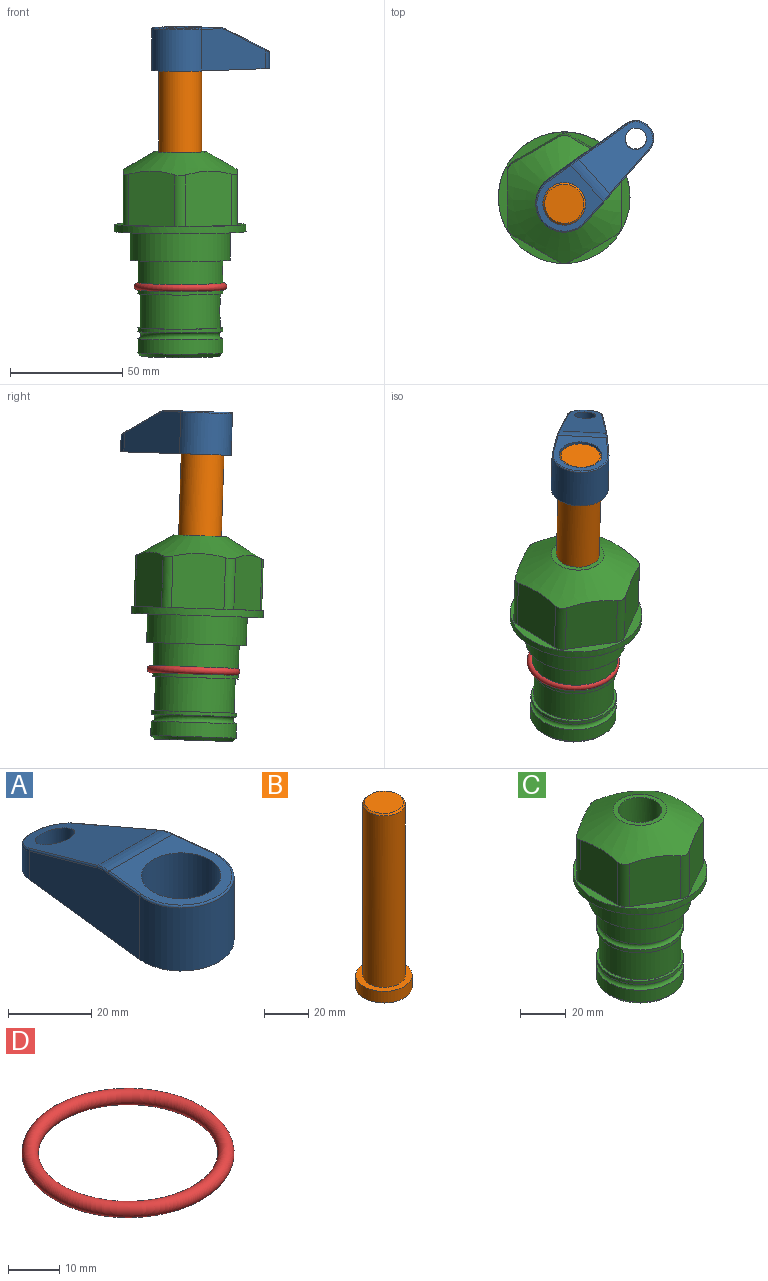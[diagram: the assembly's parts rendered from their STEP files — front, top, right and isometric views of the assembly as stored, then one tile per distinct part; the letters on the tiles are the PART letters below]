
ASSEMBLY  parts=4 mates=2
PART A: 44 faces, bbox 27.5x64.5x19.1 mm
  f0: plane 2.3x0.95mm, normal (0,0,-1), area 1mm2, adj f25,f30,f34
  f1: plane 63.5x25.4mm, normal (0,0,-1), area 561.7mm2, adj f2,f3,f4,f5,f6,f7,f19,f20
  f2: cylinder r=12.7mm len=25.4mm, axis (0,0,-1), area 792.2mm2, adj f1,f3,f5,f13
  f3: plane 42.33x18.54mm, normal (0.99,0.11,0), area 647mm2, adj f1,f2,f4,f11,f12,f14
  f4: cylinder r=7.94mm len=15.78mm, axis (0,0,-1), area 158.6mm2, adj f1,f3,f5,f16
  f5: plane 42.33x18.54mm, normal (-0.99,0.11,0), area 647mm2, adj f1,f2,f4,f15,f17,f18
  f6: cylinder r=9.53mm len=19.05mm, axis (0,0,-1), area 1140.1mm2, adj f1,f8
  f7: cylinder r=4.76mm len=10.98mm, axis (0,0,-1), area 276.1mm2, adj f1,f9
  f8: plane 25.83x24.38mm, normal (0,0,1), area 262.2mm2, adj f6,f10,f11,f13,f15
  f9: plane 32.49x20.55mm, normal (0,0.34,0.94), area 489.9mm2, adj f7,f10,f14,f16,f18
  f10: cylinder r=12.7mm len=21.49mm, axis (-1,0,0), area 93.2mm2, adj f8,f9,f12,f17
  f11: cylinder r=0.51mm len=12.34mm, axis (0.11,-0.99,0), area 9.9mm2, adj f3,f8,f12,f13
  f12: bspline ~7.62x1.64mm, area 3.5mm2, adj f3,f10,f11,f14
  f13: torus R=12.19mm, axis (0,0,1), area 33.6mm2, adj f2,f8,f11,f15
  f14: cylinder r=0.51mm len=26.01mm, axis (0.1,-0.93,0.34), area 21.6mm2, adj f3,f9,f12,f16
  f15: cylinder r=0.51mm len=12.34mm, axis (0.11,0.99,0), area 9.9mm2, adj f5,f8,f13,f17
  f16: bspline ~15.78x7.05mm, area 15.7mm2, adj f4,f9,f14,f18
  f17: bspline ~7.62x1.64mm, area 3.5mm2, adj f5,f10,f15,f18
  f18: cylinder r=0.51mm len=26.01mm, axis (0.1,0.93,-0.34), area 21.6mm2, adj f5,f9,f16,f17
  f19: plane 21.6x14.29mm, normal (-0.99,-0.11,0), area 242.6mm2, adj f1,f26,f28,f34,f36,f38
  f20: plane 21.6x14.29mm, normal (0.99,-0.11,0), area 242.6mm2, adj f1,f27,f29,f37,f39,f41
  f21: cylinder r=12.7mm len=14.29mm, axis (0,0,-1), area 173.2mm2, adj f1,f26,f27,f30,f31,f33
  f22: cylinder r=7.94mm len=7.63mm, axis (0,0,-1), area 53.8mm2, adj f1,f28,f29,f42
  f23: plane 2.3x0.95mm, normal (0,0,-1), area 1mm2, adj f25,f33,f37
  f24: plane 17.94x12.32mm, normal (0,-0.34,-0.94), area 191.2mm2, adj f25,f38,f41,f42
  f25: cylinder r=9.53mm len=12.93mm, axis (-1,0,0), area 37.5mm2, adj f0,f23,f24,f31,f36,f39
  f26: cylinder r=1.59mm len=14.29mm, axis (0,0,-1), area 49mm2, adj f1,f19,f21,f32
  f27: cylinder r=1.59mm len=14.29mm, axis (0,0,-1), area 49mm2, adj f1,f20,f21,f35
  f28: cylinder r=1.59mm len=7.28mm, axis (0,0,-1), area 22.1mm2, adj f1,f19,f22,f40
  f29: cylinder r=1.59mm len=7.28mm, axis (0,0,-1), area 22.1mm2, adj f1,f20,f22,f43
  f30: torus R=14.29mm, axis (0,0,1), area 5.8mm2, adj f0,f21,f31,f32
  f31: bspline ~11.06x2.73mm, area 20.8mm2, adj f21,f25,f30,f33
  f32: sphere r=1.59mm, area 5.4mm2, adj f26,f30,f34
  f33: torus R=14.29mm, axis (0,0,1), area 5.8mm2, adj f21,f23,f31,f35
  f34: cylinder r=1.59mm len=1.68mm, axis (-0.11,0.99,0), area 2.4mm2, adj f0,f19,f32,f36
  f35: sphere r=1.59mm, area 5.4mm2, adj f27,f33,f37
  f36: bspline ~5.82x2.33mm, area 7.7mm2, adj f19,f25,f34,f38
  f37: cylinder r=1.59mm len=1.68mm, axis (0.11,0.99,0), area 2.4mm2, adj f20,f23,f35,f39
  f38: cylinder r=1.59mm len=18.33mm, axis (0.1,-0.93,0.34), area 46.7mm2, adj f19,f24,f36,f40
  f39: bspline ~5.82x2.33mm, area 7.7mm2, adj f20,f25,f37,f41
  f40: sphere r=1.59mm, area 3.6mm2, adj f28,f38,f42
  f41: cylinder r=1.59mm len=18.33mm, axis (0.1,0.93,-0.34), area 46.7mm2, adj f20,f24,f39,f43
  f42: bspline ~8.31x1.84mm, area 15.3mm2, adj f22,f24,f40,f43
  f43: sphere r=1.59mm, area 3.6mm2, adj f29,f41,f42
PART B: 6 faces, bbox 25.4x25.4x101.6 mm
  f0: plane 17.46x17.46mm, normal (0,0,1), area 239.5mm2, adj f5
  f1: plane 25.4x25.4mm, normal (0,0,-1), area 506.7mm2, adj f2
  f2: cylinder r=12.7mm len=25.4mm, axis (0,0,1), area 506.7mm2, adj f1,f3
  f3: plane 25.4x25.4mm, normal (0,0,1), area 221.7mm2, adj f2,f4
  f4: cylinder r=9.53mm len=94.46mm, axis (0,0,1), area 5653mm2, adj f3,f5
  f5: cone r=8.73mm half-angle=45deg, axis (0,0,-1), area 64.4mm2, adj f0,f4
PART C: 36 faces, bbox 58.7x58.7x91.2 mm
  f0: cylinder r=17.78mm len=35.56mm, axis (0,0,1), area 1670.8mm2, adj f23,f24,f31
  f1: cylinder r=19.05mm len=38.1mm, axis (0,0,1), area 1191.9mm2, adj f26,f27,f30
  f2: plane 58.66x58.66mm, normal (0,0,-1), area 1150.6mm2, adj f3,f28
  f3: cylinder r=29.33mm len=58.66mm, axis (0,0,-1), area 585.1mm2, adj f2,f4
  f4: plane 58.66x58.66mm, normal (0,0,1), area 475.9mm2, adj f3,f5,f6,f7,f8,f9,f10,f11
  f5: plane 24.5x20.32mm, normal (-0.5,0.87,0), area 562.8mm2, adj f4,f15,f16,f17
  f6: plane 24.5x20.32mm, normal (0.5,0.87,0), area 562.8mm2, adj f4,f14,f15,f17
  f7: plane 24.5x23.48mm, normal (1,0,0), area 562.8mm2, adj f4,f13,f14,f17
  f8: plane 24.5x20.32mm, normal (0.5,-0.87,0), area 562.8mm2, adj f4,f12,f13,f17
  f9: plane 24.5x20.32mm, normal (-0.5,-0.87,0), area 562.8mm2, adj f4,f11,f12,f17
  f10: plane 24.5x23.48mm, normal (-1,0,0), area 562.8mm2, adj f4,f11,f16,f17
  f11: cylinder r=5.08mm len=23.01mm, axis (0,0,-1), area 121.2mm2, adj f4,f9,f10,f17
  f12: cylinder r=5.08mm len=23.01mm, axis (0,0,-1), area 121.2mm2, adj f4,f8,f9,f17
  f13: cylinder r=5.08mm len=23.01mm, axis (0,0,-1), area 121.2mm2, adj f4,f7,f8,f17
  f14: cylinder r=5.08mm len=23.01mm, axis (0,0,-1), area 121.2mm2, adj f4,f6,f7,f17
  f15: cylinder r=5.08mm len=23.01mm, axis (0,0,-1), area 121.2mm2, adj f4,f5,f6,f17
  f16: cylinder r=5.08mm len=23.01mm, axis (0,0,-1), area 121.2mm2, adj f4,f5,f10,f17
  f17: cone r=11.73mm half-angle=60deg, axis (0,0,-1), area 2071.8mm2, adj f5,f6,f7,f8,f9,f10,f11,f12
  f18: plane 23.46x23.46mm, normal (0,0,1), area 147.4mm2, adj f17,f35
  f19: plane 34.93x34.93mm, normal (0,0,-1), area 958mm2, adj f29
  f20: cylinder r=19.05mm len=38.1mm, axis (0,0,1), area 760.1mm2, adj f21,f29
  f21: torus R=19.05mm, axis (0,0,1), area 565.3mm2, adj f20,f22
  f22: cylinder r=19.05mm len=38.1mm, axis (0,0,1), area 190mm2, adj f21,f23
  f23: plane 38.1x38.1mm, normal (0,0,1), area 146.9mm2, adj f0,f22
  f24: plane 38.1x38.1mm, normal (0,0,-1), area 146.9mm2, adj f0,f25
  f25: cylinder r=19.05mm len=38.1mm, axis (0,0,1), area 190mm2, adj f24,f26
  f26: torus R=19.05mm, axis (0,0,1), area 565.3mm2, adj f1,f25
  f27: plane 44.45x44.45mm, normal (0,0,-1), area 411.7mm2, adj f1,f28
  f28: cylinder r=22.23mm len=44.45mm, axis (0,0,1), area 1773.5mm2, adj f2,f27
  f29: cone r=19.05mm half-angle=45deg, axis (0,0,1), area 257.5mm2, adj f19,f20
  f30: cylinder r=3.17mm len=6.75mm, axis (-1,0,0), area 128mm2, adj f1,f33
  f31: cylinder r=3.17mm len=6.35mm, axis (-1,0,0), area 102.5mm2, adj f0,f33
  f32: plane 25.4x25.4mm, normal (0,0,1), area 506.7mm2, adj f33
  f33: cylinder r=12.7mm len=66.42mm, axis (0,0,-1), area 5236.2mm2, adj f30,f31,f32,f34
  f34: cone r=9.53mm half-angle=30deg, axis (0,0,-1), area 443.4mm2, adj f33,f35
  f35: cylinder r=9.53mm len=19.05mm, axis (0,0,-1), area 849mm2, adj f18,f34
PART D: 1 faces, bbox 44.7x44.7x3.2 mm
  f0: torus R=19.05mm, axis (0,0,1), area 1193.9mm2
PLACE A rot(axis=(0.04,0.02,-1),48.1deg) t=(-55.19,-20.41,53.2)mm
PLACE B rot(axis=(0.04,0.02,-1),48.1deg) t=(-55.19,-18.62,-1.89)mm
PLACE C rot(axis=(1,0,0),1.9deg) t=(-55.19,-18.08,-18.65)mm fixed
PLACE D rot(axis=(1,0,0),1.9deg) t=(-55.08,-17.13,-18.62)mm
MATE cylindrical B.f2 <-> C.f0  axis (0,-0.03,1) through (-55.19,-19.46,23.73)mm
MATE fastened A.f2 <-> B.f2  axis (0,0.03,-1) through (-55.19,-21.02,71.73)mm
